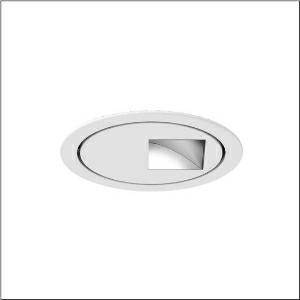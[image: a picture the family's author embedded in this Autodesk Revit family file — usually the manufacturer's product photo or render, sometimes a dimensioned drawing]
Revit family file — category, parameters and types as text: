
# Revit family: lunis_11_mini_round_51dk11cd2wn21
name_source: partatom
category: Lighting Fixtures
units: mm (PartAtom-declared; Revit-internal decimal feet)

## family parameters
Cut with Voids When Loaded = No
Host = Face
Light Source = No
Part Type = Normal
Room Calculation Point = No
Round Connector Dimension = Use Diameter
Shared = No

## types (1)
- Lunis 11 mini round (1 x LED 4000K / CRI = 90 (unbekannt), 2120 lm, 4000K)
    Apparent Load = 28 VA
    CIE Flux Codes = 44 77 97 100 100
    Color Rendering = 90
    Color Temperature = 4000K
    Default Elevation = 1800 mm
    Description = Lunis 11 mini round, downlight, light control with wallwasher, of highly reflective aluminium, highly specular, light emission: direct distribution, LED rated luminous flux: 2.120lm, light colour: 940, control gear: ECG, with terminal, 5-pole, mains connection: 220..230V, AC/DC, 0/50..60Hz, LED module, luminaire module, of aluminium, highly specular, white, diameter: 176mm, clamping range: 1..40mm, recessing ring, of plastic, traffic white (RAL 9016), protection rating (complete): IP20, insulation class (complete): insulation class II (safety insulation), certification: CE, permissible ambient temperature for indoor applications: 0..+35°C, packaging unit: 1 piece
    Height = 0 mm  [stored 0 ft]
    Lamp = 1 x LED 4000K / CRI >= 90 (unbekannt)
    Lamp Light Flux = 2120 lm
    Lamp count = 1
    Length = 176 mm
    Luminous efficacy = 76 lm/W
    Manufacturer = Siteco
    ModVariant = No
    Model = 51DK11CD2WN21
    Mounting Place = Ceiling
    Mounting Type = Recessed
    Number of Poles = 1
    OnlyDefault = Yes
    Power Factor = 1
    Product Name = Lunis 11 mini round
    Product group = downlight
    ProductGroupID = 401
    Protection Class = Protection class II
    Protection Degree = IP 20
    RLX_Detail_Level = 1
    RLX_Emergency_Light_Flux = 0 lm
    RLX_Emergency_Type = 0
    RLX_Emergency_Type_DB = No
    RlxData = <blob elided: 59505 chars, md5=3d8382c5>
    Socket = socket
    Standby Power = 0 W
    System Light Flux = 2120 lm
    System Power = 28 W
    Type Comments = Product without accessories
    Type Image = l_1004772.jpg
    URL = http://relux.com
    VarID = ---
    Voltage = 0 V
    Weight = 0.00 kg
    Width = 176 mm

note: [stored X ft] marks values corroborated as IEEE doubles in the binary element streams (Revit-internal decimal feet)

## geometry (parser evidence)
native form markers: Blend x4, Sweep x9
no freeform markers — native parametric forms only
